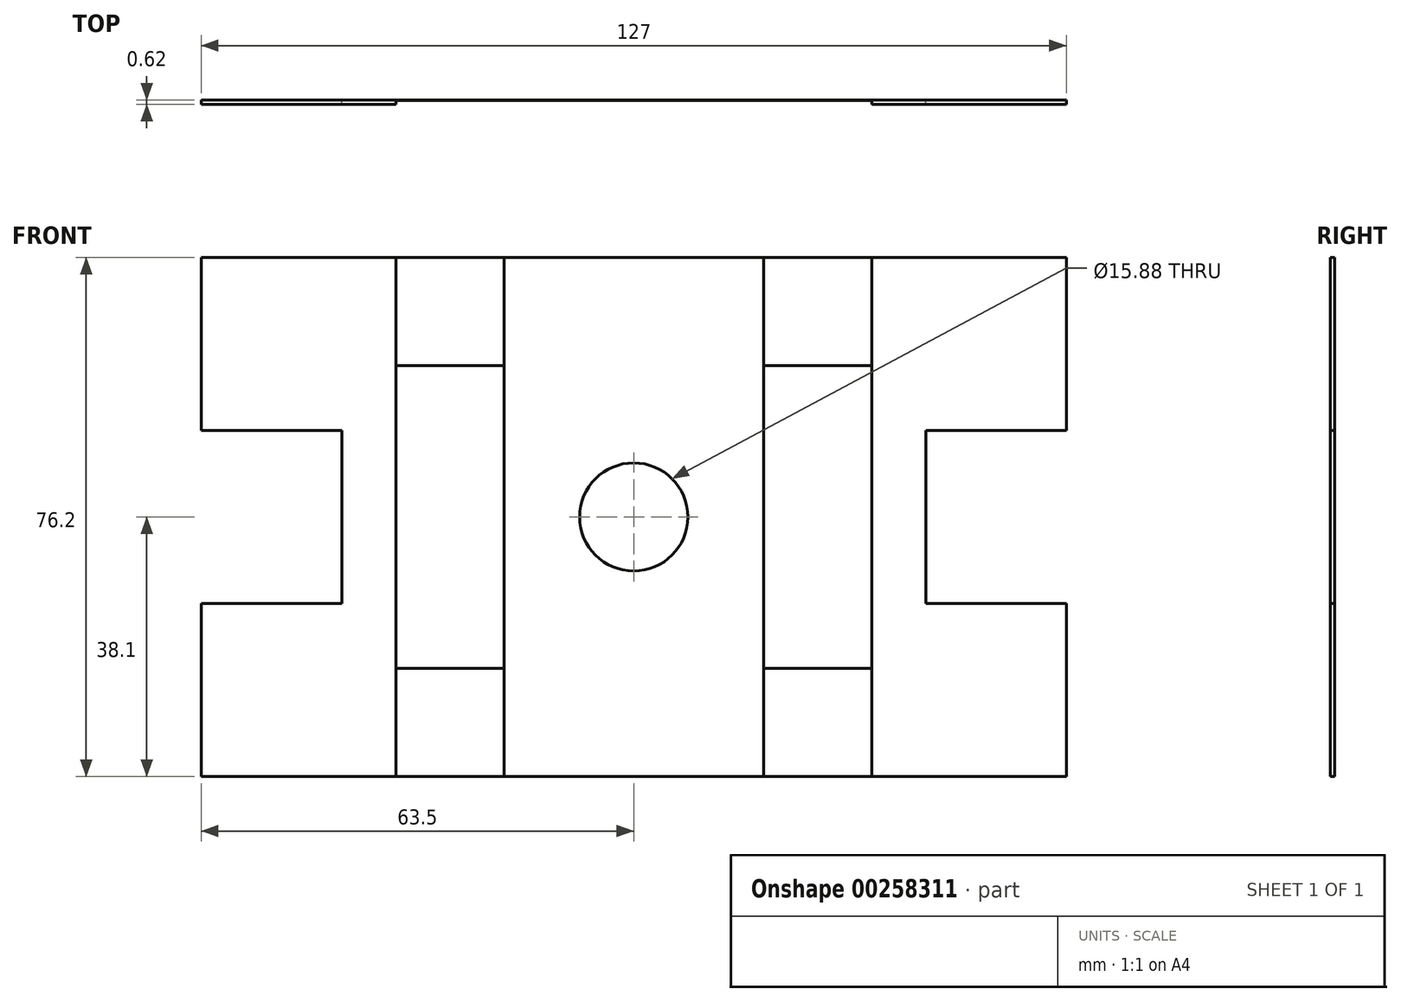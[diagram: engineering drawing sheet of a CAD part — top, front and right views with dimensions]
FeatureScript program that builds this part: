
annotation { "Feature Type Name" : "Feature", "Feature Type Description" : "" }
export const myFeature = defineFeature(function(context is Context, id is Id, definition is map)
    precondition{}
    {
        {
            var Q0;
            Q0=qCreatedBy(makeId("Front.planeOp"),FACE);
            var sketch = newSketch(context, id + "F0", { "sketchPlane" : qUnion([Q0])});
            skLineSegment(sketch, "E0.bottom", {"start": v(-63.5, 38.1) * mm, "end": v(63.5, 38.1) * mm});
            skLineSegment(sketch, "E0.top", {"start": v(-63.5, -38.1) * mm, "end": v(63.5, -38.1) * mm});
            skLineSegment(sketch, "E0.left", {"start": v(-63.5, 38.1) * mm, "end": v(-63.5, 12.7) * mm});
            skLineSegment(sketch, "E0.right", {"start": v(63.5, 38.1) * mm, "end": v(63.5, 12.7) * mm});
            skPoint(sketch, "E0.middle", {"position": v(0, 0) * mm});
            skLineSegment(sketch, "E1", {"start": v(-34.92, 38.1) * mm, "end": v(-34.92, -38.1) * mm});
            skLineSegment(sketch, "E2", {"start": v(-19.05, 38.1) * mm, "end": v(-19.05, -38.1) * mm});
            skLineSegment(sketch, "E3", {"start": v(19.05, 38.1) * mm, "end": v(19.05, -38.1) * mm});
            skLineSegment(sketch, "E4", {"start": v(34.93, 38.1) * mm, "end": v(34.93, -38.1) * mm});
            skLineSegment(sketch, "E5", {"start": v(-34.92, 22.22) * mm, "end": v(-19.05, 22.22) * mm});
            skLineSegment(sketch, "E6", {"start": v(-34.92, -22.23) * mm, "end": v(-19.05, -22.23) * mm});
            skLineSegment(sketch, "E7", {"start": v(19.05, 22.22) * mm, "end": v(34.93, 22.22) * mm});
            skLineSegment(sketch, "E8", {"start": v(19.05, -22.23) * mm, "end": v(34.93, -22.23) * mm});
            skCircle(sketch, "E9", {"center": v(0, 0) * mm, "radius": 7.94 * mm});
            skLineSegment(sketch, "E10.bottom", {"start": v(-63.5, 12.7) * mm, "end": v(-42.86, 12.7) * mm});
            skLineSegment(sketch, "E10.top", {"start": v(-63.5, -12.7) * mm, "end": v(-42.86, -12.7) * mm});
            skLineSegment(sketch, "E10.right", {"start": v(-42.86, 12.7) * mm, "end": v(-42.86, -12.7) * mm});
            skLineSegment(sketch, "E11.trimOffspring", {"start": v(-63.5, -12.7) * mm, "end": v(-63.5, -38.1) * mm});
            skLineSegment(sketch, "E12.bottom", {"start": v(63.5, 12.7) * mm, "end": v(42.85, 12.7) * mm});
            skLineSegment(sketch, "E12.top", {"start": v(63.5, -12.7) * mm, "end": v(42.85, -12.7) * mm});
            skLineSegment(sketch, "E12.right", {"start": v(42.85, 12.7) * mm, "end": v(42.85, -12.7) * mm});
            skLineSegment(sketch, "E13.trimOffspring", {"start": v(63.5, -12.7) * mm, "end": v(63.5, -38.1) * mm});
            skSolve(sketch);
        }
        {
            var Q0;
            Q0=makeQuery(id+"F0.imprint","IMPRINT",FACE,{"disambiguationData":[TD([[makeQuery(id+"F0.imprint","IMPRINT",EDGE,{"derivedFrom":sQuery(id+"F0.wireOp",EDGE,"E9")}),-1.0]])]});
            extrude(context, id + "F1", {"entities" : qUnion([Q0]), "depth" : 2.12 / 50.8 * mm});
        }
        {
            var Q0;
            {var subQ7=sQuery(id+"F0.wireOp",EDGE,"E0.left");Q0=makeQuery(id+"F0.imprint","IMPRINT",FACE,{"disambiguationData":[TD([[makeQuery(id+"F0.imprint","IMPRINT",EDGE,{"derivedFrom":subQ7}),1.0]])]});}
            var Q1;
            {var subQ0=sQuery(id+"F0.wireOp",EDGE,"E0.right");Q1=makeQuery(id+"F0.imprint","IMPRINT",FACE,{"disambiguationData":[TD([[makeQuery(id+"F0.imprint","IMPRINT",EDGE,{"derivedFrom":subQ0}),-1.0]])]});}
            extrude(context, id + "F2", {"entities" : qUnion([Q0, Q1]), "operationType" : NewBodyOperationType.ADD, "depth" : ((1.25) / 2) * mm});
        }
        {
            var Q0;
            {var subQ0=sQuery(id+"F0.wireOp",EDGE,"E5");Q0=makeQuery(id+"F0.imprint","IMPRINT",FACE,{"disambiguationData":[TD([[makeQuery(id+"F0.imprint","IMPRINT",EDGE,{"derivedFrom":subQ0}),-1.0]])]});}
            var Q1;
            {var subQ0=sQuery(id+"F0.wireOp",EDGE,"E7");Q1=makeQuery(id+"F0.imprint","IMPRINT",FACE,{"disambiguationData":[TD([[makeQuery(id+"F0.imprint","IMPRINT",EDGE,{"derivedFrom":subQ0}),-1.0]])]});}
            extrude(context, id + "F3", {"entities" : qUnion([Q0, Q1]), "operationType" : NewBodyOperationType.ADD, "depth" : 2.88 / 50.8 * mm});
        }
        {
            var Q0;
            {var subQ5=sQuery(id+"F0.wireOp",EDGE,"E5");Q0=makeQuery(id+"F0.imprint","IMPRINT",FACE,{"disambiguationData":[TD([[makeQuery(id+"F0.imprint","IMPRINT",EDGE,{"derivedFrom":subQ5}),1.0]])]});}
            var Q1;
            {var subQ5=sQuery(id+"F0.wireOp",EDGE,"E7");Q1=makeQuery(id+"F0.imprint","IMPRINT",FACE,{"disambiguationData":[TD([[makeQuery(id+"F0.imprint","IMPRINT",EDGE,{"derivedFrom":subQ5}),1.0]])]});}
            var Q2;
            {var subQ5=sQuery(id+"F0.wireOp",EDGE,"E8");Q2=makeQuery(id+"F0.imprint","IMPRINT",FACE,{"disambiguationData":[TD([[makeQuery(id+"F0.imprint","IMPRINT",EDGE,{"derivedFrom":subQ5}),-1.0]])]});}
            var Q3;
            {var subQ5=sQuery(id+"F0.wireOp",EDGE,"E6");Q3=makeQuery(id+"F0.imprint","IMPRINT",FACE,{"disambiguationData":[TD([[makeQuery(id+"F0.imprint","IMPRINT",EDGE,{"derivedFrom":subQ5}),-1.0]])]});}
            extrude(context, id + "F4", {"entities" : qUnion([Q0, Q1, Q2, Q3]), "operationType" : NewBodyOperationType.ADD, "depth" : (3 + 5 / 8) / 50.8 * mm});
        }
    });
